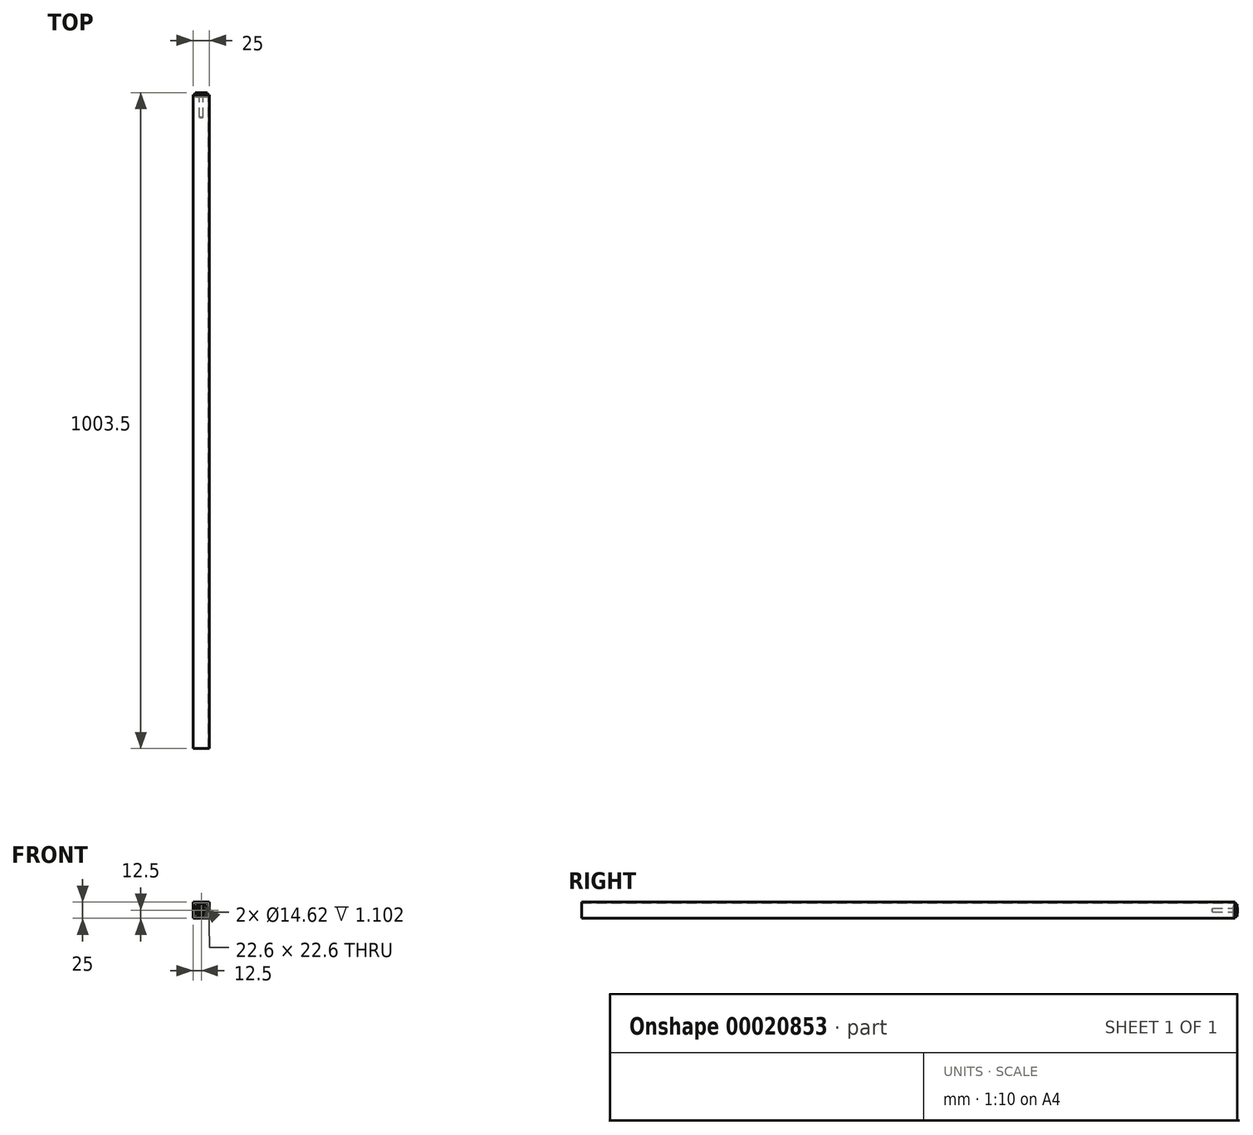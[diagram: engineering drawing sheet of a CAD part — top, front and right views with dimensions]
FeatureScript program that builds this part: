
annotation { "Feature Type Name" : "Feature", "Feature Type Description" : "" }
export const myFeature = defineFeature(function(context is Context, id is Id, definition is map)
    precondition{}
    {
        {
            assignVariable(context, id + "F0", {"variableType" : VariableType.LENGTH, "name" : "Epaisseur", "lengthValue" : 6 * mm});
        }
        {
            var Q0;
            Q0=qCreatedBy(makeId("Front.planeOp"),FACE);
            var sketch = newSketch(context, id + "F1", { "sketchPlane" : qUnion([Q0])});
            skCircle(sketch, "E0", {"center": v(0, 0) * mm, "radius": 2.93 * mm});
            skCircle(sketch, "E1", {"center": v(0, 0) * mm, "radius": 9.5 * mm});
            skCircle(sketch, "E2", {"center": v(0, 0) * mm, "radius": 5.12 * mm});
            skCircle(sketch, "E3", {"center": v(0, 0) * mm, "radius": 7.3 * mm});
            skLineSegment(sketch, "E4", {"start": v(0, 5.12) * mm, "end": v(0, 7.3) * mm, "construction": true});
            skPoint(sketch, "E5", {"position": v(0, 6.21) * mm});
            skLineSegment(sketch, "E6", {"start": v(0, -13.46) * mm, "end": v(0, 19.25) * mm, "construction": true});
            skSolve(sketch);
        }
        {
            var Q0;
            Q0=makeQuery(id+"F1.imprint","IMPRINT",FACE,{"disambiguationData":[TD([[makeQuery(id+"F1.imprint","IMPRINT",EDGE,{"derivedFrom":sQuery(id+"F1.wireOp",EDGE,"E0")}),-1.0]])]});
            extrude(context, id + "F2", {"entities" : qUnion([Q0]), "endBound" : BoundingType.SYMMETRIC, "offsetDistance" : 25 * mm, "depth" : getVariable(context, 'Epaisseur'), "hasSecondDirection" : true, "secondDirectionOppositeDirection" : true, "secondDirectionDepth" : 2.5 * mm});
        }
        {
            var Q0;
            Q0 = qSketchRegion(id + "F1", true);
            var Q1;
            Q1=makeQuery(id+"F2.opExtrude","CAP_FACE",FACE,{"disambiguationData":[OSD([sQuery(id+"F1.wireOp",EDGE,"E0"),sQuery(id+"F1.wireOp",EDGE,"E2")])],"isStart":false});
            var Q2;
            Q2=makeQuery(id+"F2.opExtrude","CAP_FACE",FACE,{"disambiguationData":[OSD([sQuery(id+"F1.wireOp",EDGE,"E0"),sQuery(id+"F1.wireOp",EDGE,"E2")])],"isStart":true});
            extrude(context, id + "F3", {"entities" : qUnion([Q0]), "endBound" : BoundingType.SYMMETRIC, "endBoundEntityFace" : qUnion([Q1]), "offsetDistance" : 25 * mm, "depth" : getVariable(context, 'Epaisseur'), "hasSecondDirection" : true, "secondDirectionBound" : SecondDirectionBoundingType.UP_TO_SURFACE, "secondDirectionOppositeDirection" : true, "secondDirectionBoundEntityFace" : qUnion([Q2]), "secondDirectionDepth" : 25 * mm});
        }
        {
            var Q0;
            Q0=qCreatedBy(makeId("Right.planeOp"),FACE);
            var sketch = newSketch(context, id + "F4", { "sketchPlane" : qUnion([Q0])});
            skCircle(sketch, "E7", {"center": v(0, 6.21) * mm, "radius": 2.2 * mm});
            skLineSegment(sketch, "E8", {"start": v(0, 0) * mm, "end": v(0, 13.37) * mm, "construction": true});
            skSolve(sketch);
        }
        {
            var Q0;
            Q0=makeQuery(id+"F4.imprint","IMPRINT",FACE,{"disambiguationData":[TD([[makeQuery(id+"F4.imprint","IMPRINT",EDGE,{"derivedFrom":sQuery(id+"F4.wireOp",EDGE,"E7")}),1.0]])]});
            var Q1;
            Q1=makeQuery(id+"F2.opExtrude","SWEPT_FACE",FACE,{"disambiguationData":[OSD([sQuery(id+"F1.wireOp",EDGE,"E0")])]});
            revolve(context, id + "F5", {"operationType" : NewBodyOperationType.REMOVE, "entities" : qUnion([Q0]), "axis" : qUnion([Q1]), "revolveType" : RevolveType.FULL, "oppositeDirection" : true});
        }
        {
            var Q0;
            Q0=makeQuery(id+"F4.imprint","IMPRINT",FACE,{"disambiguationData":[TD([[makeQuery(id+"F4.imprint","IMPRINT",EDGE,{"derivedFrom":sQuery(id+"F4.wireOp",EDGE,"E7")}),1.0]])]});
            var Q1;
            Q1=makeQuery(id+"F2.opExtrude","SWEPT_FACE",FACE,{"disambiguationData":[OSD([sQuery(id+"F1.wireOp",EDGE,"E0")])]});
            revolve(context, id + "F6", {"entities" : qUnion([Q0]), "axis" : qUnion([Q1]), "revolveType" : RevolveType.FULL});
        }
        {
            var Q0;
            Q0=makeQuery(id+"F1.imprint","IMPRINT",FACE,{"disambiguationData":[TD([[makeQuery(id+"F1.imprint","IMPRINT",EDGE,{"derivedFrom":sQuery(id+"F1.wireOp",EDGE,"E0")}),1.0]])]});
            extrude(context, id + "F7", {"entities" : qUnion([Q0]), "depth" : 35 * mm});
        }
        {
            var Q0;
            Q0=makeQuery(id+"F7.opExtrude","CAP_FACE",FACE,{"disambiguationData":[OSD([sQuery(id+"F1.wireOp",EDGE,"E0")])],"isStart":true});
            var sketch = newSketch(context, id + "F8", { "sketchPlane" : qUnion([Q0])});
            skCircle(sketch, "E9.cCircle", {"center": v(0, 0) * mm, "radius": 4 * mm, "construction": true});
            skLineSegment(sketch, "E9.0", {"start": v(-4, -2.3) * mm, "end": v(-4, 2.3) * mm});
            skLineSegment(sketch, "E9.1", {"start": v(-4, 2.3) * mm, "end": v(0, 4.62) * mm});
            skLineSegment(sketch, "E9.2", {"start": v(0, 4.62) * mm, "end": v(4, 2.3) * mm});
            skLineSegment(sketch, "E9.3", {"start": v(4, 2.3) * mm, "end": v(4, -2.3) * mm});
            skLineSegment(sketch, "E9.4", {"start": v(4, -2.3) * mm, "end": v(0, -4.62) * mm});
            skLineSegment(sketch, "E9.5", {"start": v(0, -4.62) * mm, "end": v(-4, -2.3) * mm});
            skPoint(sketch, "E9.0.midPoint", {"position": v(-4, 0) * mm});
            skSolve(sketch);
        }
        {
            var Q0;
            Q0 = qSketchRegion(id + "F8", true);
            extrude(context, id + "F9", {"entities" : qUnion([Q0]), "operationType" : NewBodyOperationType.ADD, "depth" : 3.5 * mm});
        }
        {
            var Q0;
            Q0=makeQuery(id+"F7.opExtrude","CAP_EDGE",EDGE,{"disambiguationData":[OSD([sQuery(id+"F1.wireOp",EDGE,"E0")])],"isStart":false});
            chamfer(context, id + "F10", {"entities" : qUnion([Q0]), "chamferType" : ChamferType.OFFSET_ANGLE, "width" : 1 * mm, "oppositeDirection" : false, "angle" : 30 * degree, "tangentPropagation" : true});
        }
        {
            var Q0;
            Q0=makeQuery(id+"F9.opExtrude","CAP_FACE",FACE,{"disambiguationData":[OSD([sQuery(id+"F8.wireOp",EDGE,"E9.0"),sQuery(id+"F8.wireOp",EDGE,"E9.1"),sQuery(id+"F8.wireOp",EDGE,"E9.2"),sQuery(id+"F8.wireOp",EDGE,"E9.3"),sQuery(id+"F8.wireOp",EDGE,"E9.4"),sQuery(id+"F8.wireOp",EDGE,"E9.5")])],"isStart":false});
            var sketch = newSketch(context, id + "F11", { "sketchPlane" : qUnion([Q0])});
            skCircle(sketch, "E10", {"center": v(0, 0) * mm, "radius": 4 * mm});
            skSolve(sketch);
        }
        {
            var Q0;
            Q0=qCreatedBy(makeId("Top.planeOp"),FACE);
            var sketch = newSketch(context, id + "F12", { "sketchPlane" : qUnion([Q0])});
            skLineSegment(sketch, "E11", {"start": v(4, 3.5) * mm, "end": v(5.42, 3.5) * mm});
            skLineSegment(sketch, "E12", {"start": v(5.42, 3.5) * mm, "end": v(5.42, 2.68) * mm});
            skLineSegment(sketch, "E13", {"start": v(5.42, 2.68) * mm, "end": v(4, 3.5) * mm});
            skSolve(sketch);
        }
        {
            var Q0;
            Q0 = qSketchRegion(id + "F12", true);
            var Q1;
            Q1=makeQuery(id+"F7.opExtrude","SWEPT_FACE",FACE,{"disambiguationData":[OSD([sQuery(id+"F1.wireOp",EDGE,"E0")])]});
            revolve(context, id + "F13", {"operationType" : NewBodyOperationType.REMOVE, "entities" : qUnion([Q0]), "axis" : qUnion([Q1]), "revolveType" : RevolveType.FULL, "oppositeDirection" : true});
        }
        {
            var Q0;
            Q0=qCreatedBy(makeId("Front.planeOp"), FACE);
            var sketch = newSketch(context, id + "F14", { "sketchPlane" : qUnion([Q0])});
            skLineSegment(sketch, "E14.bottom", {"start": v(12.5, -12.5) * mm, "end": v(-12.5, -12.5) * mm});
            skLineSegment(sketch, "E14.top", {"start": v(12.5, 12.5) * mm, "end": v(-12.5, 12.5) * mm});
            skLineSegment(sketch, "E14.left", {"start": v(12.5, -12.5) * mm, "end": v(12.5, 12.5) * mm});
            skLineSegment(sketch, "E14.right", {"start": v(-12.5, -12.5) * mm, "end": v(-12.5, 12.5) * mm});
            skPoint(sketch, "E14.middle", {"position": v(0, 0) * mm});
            skLineSegment(sketch, "E15.bottom", {"start": v(11.3, -11.3) * mm, "end": v(-11.3, -11.3) * mm});
            skLineSegment(sketch, "E15.top", {"start": v(11.3, 11.3) * mm, "end": v(-11.3, 11.3) * mm});
            skLineSegment(sketch, "E15.left", {"start": v(11.3, -11.3) * mm, "end": v(11.3, 11.3) * mm});
            skLineSegment(sketch, "E15.right", {"start": v(-11.3, -11.3) * mm, "end": v(-11.3, 11.3) * mm});
            skSolve(sketch);
        }
        {
            var Q0;
            Q0 = qSketchRegion(id + "F14", true);
            extrude(context, id + "F15", {"entities" : qUnion([Q0]), "depth" : 1000 * mm, "offsetDistance" : 25 * mm});
        }
    });
